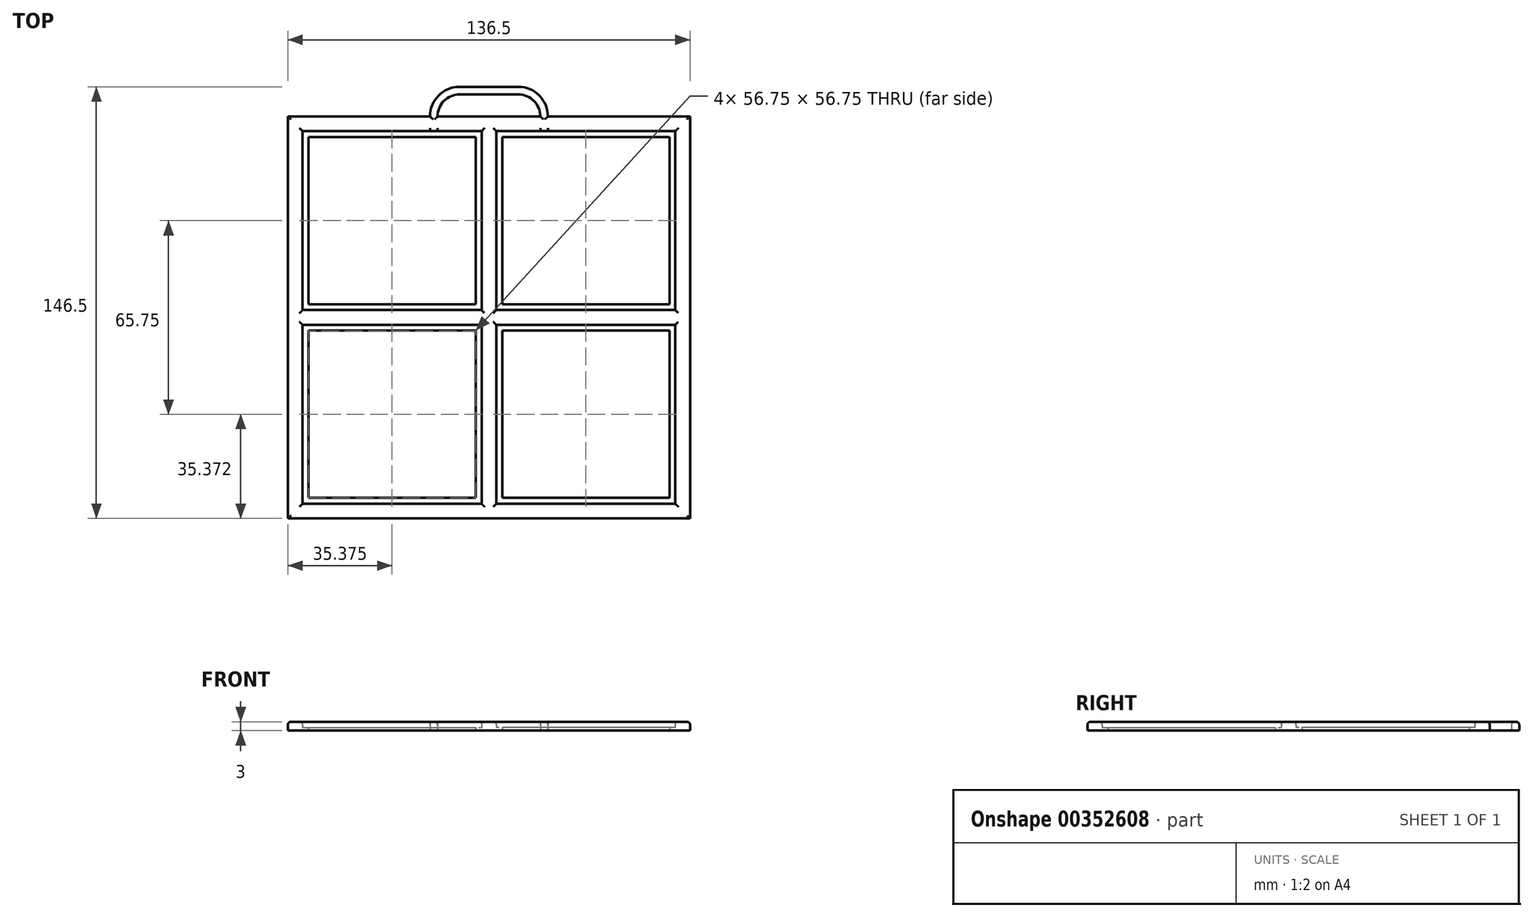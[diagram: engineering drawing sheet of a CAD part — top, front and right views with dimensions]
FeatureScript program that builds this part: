
annotation { "Feature Type Name" : "Feature", "Feature Type Description" : "" }
export const myFeature = defineFeature(function(context is Context, id is Id, definition is map)
    precondition{}
    {
        {
            var Q0;
            Q0=qCreatedBy(makeId("Top.planeOp"),FACE);
            var sketch = newSketch(context, id + "F0", { "sketchPlane" : qUnion([Q0])});
            skLineSegment(sketch, "E0.bottom", {"start": v(-63.25, 26.55) * mm, "end": v(-2.5, 26.55) * mm});
            skLineSegment(sketch, "E0.top", {"start": v(-63.25, -34.2) * mm, "end": v(-2.5, -34.2) * mm});
            skLineSegment(sketch, "E0.left", {"start": v(-63.25, 26.55) * mm, "end": v(-63.25, -34.2) * mm});
            skLineSegment(sketch, "E0.right", {"start": v(-2.5, 26.55) * mm, "end": v(-2.5, -34.2) * mm});
            skPoint(sketch, "E1", {"position": v(-2.5, 26.55) * mm});
            skPoint(sketch, "E2", {"position": v(-2.5, 31.55) * mm});
            skPoint(sketch, "E3", {"position": v(-2.5, -34.2) * mm});
            skPoint(sketch, "E4", {"position": v(-2.5, -36.7) * mm});
            skPoint(sketch, "E5", {"position": v(-63.25, -36.7) * mm});
            skPoint(sketch, "E6", {"position": v(-63.25, 31.55) * mm});
            skPoint(sketch, "E7", {"position": v(-63.25, 26.55) * mm});
            skPoint(sketch, "E8", {"position": v(-68.25, 26.55) * mm});
            skPoint(sketch, "E9", {"position": v(-68.25, 31.55) * mm});
            skPoint(sketch, "E10", {"position": v(0, -36.7) * mm});
            skLineSegment(sketch, "E11.bottom", {"start": v(-68.25, 31.55) * mm, "end": v(-20, 31.55) * mm});
            skLineSegment(sketch, "E11.top", {"start": v(-68.25, -36.7) * mm, "end": v(0, -36.7) * mm});
            skLineSegment(sketch, "E11.left", {"start": v(-68.25, 31.55) * mm, "end": v(-68.25, -36.7) * mm});
            skLineSegment(sketch, "E11.right", {"start": v(0, 31.55) * mm, "end": v(0, -36.7) * mm});
            skPoint(sketch, "E12", {"position": v(-34.12, 31.55) * mm});
            skPoint(sketch, "E13", {"position": v(-34.12, 41.55) * mm});
            skLineSegment(sketch, "E14", {"start": v(-34.12, 41.55) * mm, "end": v(-34.12, 31.55) * mm});
            skPoint(sketch, "E15", {"position": v(-34.12, 36.55) * mm});
            skPoint(sketch, "E16", {"position": v(-34.12, 38.98) * mm});
            skPoint(sketch, "E17", {"position": v(-61.25, 26.55) * mm});
            skPoint(sketch, "E18", {"position": v(-63.25, 24.55) * mm});
            skPoint(sketch, "E19", {"position": v(-61.25, 24.55) * mm});
            skPoint(sketch, "E20", {"position": v(-2.5, -32.2) * mm});
            skPoint(sketch, "E21", {"position": v(-4.5, -34.2) * mm});
            skPoint(sketch, "E22", {"position": v(-4.5, -32.2) * mm});
            skLineSegment(sketch, "E23.bottom", {"start": v(-61.25, 24.55) * mm, "end": v(-4.5, 24.55) * mm});
            skLineSegment(sketch, "E23.top", {"start": v(-61.25, -32.2) * mm, "end": v(-4.5, -32.2) * mm});
            skLineSegment(sketch, "E23.left", {"start": v(-61.25, 24.55) * mm, "end": v(-61.25, -32.2) * mm});
            skLineSegment(sketch, "E23.right", {"start": v(-4.5, 24.55) * mm, "end": v(-4.5, -32.2) * mm});
            skPoint(sketch, "E24", {"position": v(-10, 31.55) * mm});
            skLineSegment(sketch, "E25", {"start": v(0, 38.98) * mm, "end": v(0, 41.55) * mm});
            skPoint(sketch, "E26", {"position": v(-10, 38.98) * mm});
            skPoint(sketch, "E27", {"position": v(-10, 41.55) * mm});
            skArc(sketch, "E28", {"start": v(-10, 38.98) * mm, "mid": v(-15.25, 36.8) * mm, "end": v(-17.43, 31.55) * mm});
            skArc(sketch, "E29", {"start": v(-10, 41.55) * mm, "mid": v(-17.07, 38.62) * mm, "end": v(-20, 31.55) * mm});
            skLineSegment(sketch, "E30", {"start": v(-10, 38.98) * mm, "end": v(0, 38.98) * mm});
            skLineSegment(sketch, "E31", {"start": v(-10, 41.55) * mm, "end": v(0, 41.55) * mm});
            skLineSegment(sketch, "E32", {"start": v(-20, 31.55) * mm, "end": v(-17.43, 31.55) * mm});
            skLineSegment(sketch, "E33", {"start": v(-17.43, 31.55) * mm, "end": v(0, 31.55) * mm});
            skLineSegment(sketch, "E34", {"start": v(-20, 31.55) * mm, "end": v(-20, 26.55) * mm});
            skLineSegment(sketch, "E35", {"start": v(-20, 26.55) * mm, "end": v(-17.43, 26.55) * mm});
            skLineSegment(sketch, "E36", {"start": v(-17.43, 26.55) * mm, "end": v(-17.43, 31.55) * mm});
            skSolve(sketch);
        }
        {
            var Q0;
            Q0=makeQuery(id+"F0.imprint","IMPRINT",FACE,{"disambiguationData":[TD([[makeQuery(id+"F0.imprint","IMPRINT",EDGE,{"derivedFrom":sQuery(id+"F0.wireOp",EDGE,"E0.top")}),-1.0]])]});
            var Q1;
            {var subQ0=sQuery(id+"F0.wireOp",EDGE,"323iFSkM-69Tl-kqoX-bfbl-zxdwPlZIsCMZ");var subQ1=sQuery(id+"F0.wireOp",EDGE,"E0.bottom");var subQ2=makeQuery(id+"F0.imprint","INTERSECT",VERTEX,{"disambiguationData":[OD(0.0)],"derivedFrom":[subQ1,subQ0]});Q1=makeQuery(id+"F0.imprint","IMPRINT",FACE,{"disambiguationData":[TD([[makeQuery(id+"F0.imprint","IMPRINT",EDGE,{"disambiguationData":[TD([[subQ2,-1.0]])],"derivedFrom":subQ1}),1.0]])]});}
            var Q2;
            {var subQ0=sQuery(id+"F0.wireOp",EDGE,"S2f47POQ-odG1-F0nU-moLb-DiT50xx8mqJj");var subQ1=sQuery(id+"F0.wireOp",EDGE,"E0.bottom");var subQ2=makeQuery(id+"F0.imprint","INTERSECT",VERTEX,{"disambiguationData":[OD(1.0)],"derivedFrom":[subQ1,subQ0]});Q2=makeQuery(id+"F0.imprint","IMPRINT",FACE,{"disambiguationData":[TD([[makeQuery(id+"F0.imprint","IMPRINT",EDGE,{"disambiguationData":[TD([[subQ2,-1.0]])],"derivedFrom":subQ1}),1.0]])]});}
            var Q3;
            {var subQ0=sQuery(id+"F0.wireOp",EDGE,"S2f47POQ-odG1-F0nU-moLb-DiT50xx8mqJj");var subQ1=sQuery(id+"F0.wireOp",EDGE,"E0.bottom");var subQ2=makeQuery(id+"F0.imprint","INTERSECT",VERTEX,{"disambiguationData":[OD(0.0)],"derivedFrom":[subQ1,subQ0]});Q3=makeQuery(id+"F0.imprint","IMPRINT",FACE,{"disambiguationData":[TD([[makeQuery(id+"F0.imprint","IMPRINT",EDGE,{"disambiguationData":[TD([[subQ2,-1.0]])],"derivedFrom":subQ1}),1.0]])]});}
            var Q4;
            {var subQ0=sQuery(id+"F0.wireOp",EDGE,"RwKeYdOv-RQ1C-EBcZ-qULq-cMKYxm2aIbZM");var subQ1=sQuery(id+"F0.wireOp",EDGE,"E0.right");var subQ2=makeQuery(id+"F0.imprint","INTERSECT",VERTEX,{"derivedFrom":[subQ1,subQ0]});Q4=makeQuery(id+"F0.imprint","IMPRINT",FACE,{"disambiguationData":[TD([[makeQuery(id+"F0.imprint","IMPRINT",EDGE,{"disambiguationData":[TD([[subQ2,-1.0]])],"derivedFrom":subQ1}),1.0]])]});}
            var Q5;
            {var subQ6=sQuery(id+"F0.wireOp",EDGE,"E0.bottom");var subQ8=sQuery(id+"F0.wireOp",EDGE,"E0.right");var subQ9=makeQuery(id+"F0.imprint","INTERSECT",VERTEX,{"derivedFrom":[subQ6,subQ8]});Q5=makeQuery(id+"F0.imprint","IMPRINT",FACE,{"disambiguationData":[TD([[makeQuery(id+"F0.imprint","IMPRINT",EDGE,{"disambiguationData":[TD([[subQ9,1.0]])],"derivedFrom":subQ6}),1.0]])]});}
            var Q6;
            Q6=makeQuery(id+"F0.imprint","IMPRINT",FACE,{"disambiguationData":[TD([[makeQuery(id+"F0.imprint","IMPRINT",EDGE,{"derivedFrom":sQuery(id+"F0.wireOp",EDGE,"E32")}),-1.0]])]});
            extrude(context, id + "F1", {"entities" : qUnion([Q0, Q1, Q2, Q3, Q4, Q5, Q6]), "depth" : 3 * mm, "offsetDistance" : 25 * mm});
        }
        {
            var Q0;
            {var subQ0=sQuery(id+"F0.wireOp",EDGE,"S2f47POQ-odG1-F0nU-moLb-DiT50xx8mqJj");var subQ1=sQuery(id+"F0.wireOp",EDGE,"E0.bottom");var subQ2=makeQuery(id+"F0.imprint","INTERSECT",VERTEX,{"disambiguationData":[OD(0.0)],"derivedFrom":[subQ1,subQ0]});Q0=makeQuery(id+"F0.imprint","IMPRINT",FACE,{"disambiguationData":[TD([[makeQuery(id+"F0.imprint","IMPRINT",EDGE,{"disambiguationData":[TD([[subQ2,-1.0]])],"derivedFrom":subQ1}),-1.0]])]});}
            var Q1;
            {var subQ0=sQuery(id+"F0.wireOp",EDGE,"323iFSkM-69Tl-kqoX-bfbl-zxdwPlZIsCMZ");var subQ1=sQuery(id+"F0.wireOp",EDGE,"E0.bottom");var subQ2=makeQuery(id+"F0.imprint","INTERSECT",VERTEX,{"disambiguationData":[OD(0.0)],"derivedFrom":[subQ1,subQ0]});Q1=makeQuery(id+"F0.imprint","IMPRINT",FACE,{"disambiguationData":[TD([[makeQuery(id+"F0.imprint","IMPRINT",EDGE,{"disambiguationData":[TD([[subQ2,-1.0]])],"derivedFrom":subQ1}),-1.0]])]});}
            var Q2;
            {var subQ0=sQuery(id+"F0.wireOp",EDGE,"S2f47POQ-odG1-F0nU-moLb-DiT50xx8mqJj");var subQ1=sQuery(id+"F0.wireOp",EDGE,"E0.bottom");var subQ2=makeQuery(id+"F0.imprint","INTERSECT",VERTEX,{"disambiguationData":[OD(1.0)],"derivedFrom":[subQ1,subQ0]});Q2=makeQuery(id+"F0.imprint","IMPRINT",FACE,{"disambiguationData":[TD([[makeQuery(id+"F0.imprint","IMPRINT",EDGE,{"disambiguationData":[TD([[subQ2,-1.0]])],"derivedFrom":subQ1}),-1.0]])]});}
            var Q3;
            Q3=makeQuery(id+"F0.imprint","IMPRINT",FACE,{"disambiguationData":[TD([[makeQuery(id+"F0.imprint","IMPRINT",EDGE,{"derivedFrom":sQuery(id+"F0.wireOp",EDGE,"E0.top")}),1.0]])]});
            var Q4;
            {var subQ3=sQuery(id+"F0.wireOp",EDGE,"oISM5f6R-s7pY-zFvx-TeqI-MK5FqsrAusou");var subQ10=sQuery(id+"F0.wireOp",EDGE,"E0.bottom");var subQ11=makeQuery(id+"F0.imprint","INTERSECT",VERTEX,{"derivedFrom":[subQ10,subQ3]});Q4=makeQuery(id+"F0.imprint","IMPRINT",FACE,{"disambiguationData":[TD([[makeQuery(id+"F0.imprint","IMPRINT",EDGE,{"disambiguationData":[TD([[subQ11,-1.0]])],"derivedFrom":subQ10}),-1.0]])]});}
            extrude(context, id + "F2", {"entities" : qUnion([Q0, Q1, Q2, Q3, Q4]), "operationType" : NewBodyOperationType.ADD, "depth" : 1 * mm});
        }
        {
            var Q0;
            Q0=makeQuery(id+"F1.opExtrude","CAP_EDGE",EDGE,{"disambiguationData":[OSD([sQuery(id+"F0.wireOp",EDGE,"E0.bottom")])],"isStart":false});
            var Q1;
            Q1=makeQuery(id+"F1.opExtrude","CAP_EDGE",EDGE,{"disambiguationData":[OSD([sQuery(id+"F0.wireOp",EDGE,"E0.left")])],"isStart":false});
            var Q2;
            Q2=makeQuery(id+"F1.opExtrude","CAP_EDGE",EDGE,{"disambiguationData":[OSD([sQuery(id+"F0.wireOp",EDGE,"E0.top")])],"isStart":false});
            var Q3;
            Q3=makeQuery(id+"F1.opExtrude","CAP_EDGE",EDGE,{"disambiguationData":[OSD([sQuery(id+"F0.wireOp",EDGE,"E0.right")])],"isStart":false});
            var Q4;
            {var subQ0=sQuery(id+"F0.wireOp",EDGE,"E11.bottom");var subQ1=makeQuery(id+"F0.imprint","IMPRINT",VERTEX,{"derivedFrom":subQ0});Q4=makeQuery(id+"F1.opExtrude","CAP_EDGE",EDGE,{"disambiguationData":[OSD([subQ0]),TDD([makeQuery(id+"F0.imprint","IMPRINT",EDGE,{"disambiguationData":[TD([[subQ1,1.0]])],"derivedFrom":subQ0}),makeQuery(id+"F0.imprint","IMPRINT",EDGE,{"disambiguationData":[TD([[subQ1,-1.0]])],"derivedFrom":subQ0})])],"isStart":false});}
            var Q5;
            Q5=makeQuery(id+"F1.opExtrude","CAP_EDGE",EDGE,{"disambiguationData":[OSD([sQuery(id+"F0.wireOp",EDGE,"E11.left")])],"isStart":false});
            var Q6;
            Q6=makeQuery(id+"F1.opExtrude","CAP_EDGE",EDGE,{"disambiguationData":[OSD([sQuery(id+"F0.wireOp",EDGE,"oISM5f6R-s7pY-zFvx-TeqI-MK5FqsrAusou")])],"isStart":false});
            var Q7;
            Q7=makeQuery(id+"F1.opExtrude","CAP_EDGE",EDGE,{"disambiguationData":[OSD([sQuery(id+"F0.wireOp",EDGE,"RwKeYdOv-RQ1C-EBcZ-qULq-cMKYxm2aIbZM")])],"isStart":false});
            var Q8;
            {var subQ0=sQuery(id+"F0.wireOp",EDGE,"E11.bottom");Q8=makeQuery(id+"F1.opExtrude","CAP_EDGE",EDGE,{"disambiguationData":[OSD([subQ0]),TDD([makeQuery(id+"F0.imprint","IMPRINT",EDGE,{"disambiguationData":[TD([[makeQuery(id+"F0.imprint","INTERSECT",VERTEX,{"derivedFrom":[subQ0,sQuery(id+"F0.wireOp",EDGE,"RwKeYdOv-RQ1C-EBcZ-qULq-cMKYxm2aIbZM")]}),-1.0]])],"derivedFrom":subQ0})])],"isStart":false});}
            fillet(context, id + "F3", {"entities" : qUnion([Q0, Q1, Q2, Q3, Q4, Q5, Q6, Q7, Q8]), "radius" : 1 * mm, "tangentPropagation" : true, "allowEdgeOverflow" : false});
        }
        {
            var Q0;
            Q0=makeQuery(id+"F1.opExtrude","SWEPT_BODY",BODY,{"disambiguationData":[OSD([sQuery(id+"F0.wireOp",EDGE,"E0.bottom"),sQuery(id+"F0.wireOp",EDGE,"E0.top"),sQuery(id+"F0.wireOp",EDGE,"E0.left"),sQuery(id+"F0.wireOp",EDGE,"E0.right"),sQuery(id+"F0.wireOp",EDGE,"E11.bottom"),sQuery(id+"F0.wireOp",EDGE,"E11.top"),sQuery(id+"F0.wireOp",EDGE,"E11.left"),sQuery(id+"F0.wireOp",EDGE,"E11.right"),sQuery(id+"F0.wireOp",EDGE,"323iFSkM-69Tl-kqoX-bfbl-zxdwPlZIsCMZ"),sQuery(id+"F0.wireOp",EDGE,"S2f47POQ-odG1-F0nU-moLb-DiT50xx8mqJj")])]});
            var Q1;
            Q1=qCreatedBy(makeId("Right.planeOp"),FACE);
            mirror(context, id + "F4", {"operationType" : NewBodyOperationType.ADD, "entities" : qUnion([Q0]), "mirrorPlane" : qUnion([Q1])});
        }
        {
            var Q0;
            Q0=makeQuery(id+"F1.opExtrude","SWEPT_BODY",BODY,{"disambiguationData":[OSD([sQuery(id+"F0.wireOp",EDGE,"E0.bottom"),sQuery(id+"F0.wireOp",EDGE,"E0.top"),sQuery(id+"F0.wireOp",EDGE,"E0.left"),sQuery(id+"F0.wireOp",EDGE,"E0.right"),sQuery(id+"F0.wireOp",EDGE,"E11.bottom"),sQuery(id+"F0.wireOp",EDGE,"E11.top"),sQuery(id+"F0.wireOp",EDGE,"E11.left"),sQuery(id+"F0.wireOp",EDGE,"E11.right"),sQuery(id+"F0.wireOp",EDGE,"YFA6sMg5-ooe4-pIfk-JmcR-r9i5VlROMLmz"),sQuery(id+"F0.wireOp",EDGE,"oISM5f6R-s7pY-zFvx-TeqI-MK5FqsrAusou"),sQuery(id+"F0.wireOp",EDGE,"RwKeYdOv-RQ1C-EBcZ-qULq-cMKYxm2aIbZM")])]});
            var Q1;
            {var subQ0=makeQuery(id+"F1.opExtrude","SWEPT_FACE",FACE,{"disambiguationData":[OSD([sQuery(id+"F0.wireOp",EDGE,"E11.top")])]});Q1=makeQuery(id+"F4.boolean.opBoolean","MERGE",FACE,{"derivedFrom":[subQ0,makeQuery(id+"F4.opPattern","COPY",FACE,{"derivedFrom":subQ0,"instanceName":"1"})]});}
            mirror(context, id + "F5", {"operationType" : NewBodyOperationType.ADD, "entities" : qUnion([Q0]), "mirrorPlane" : qUnion([Q1])});
        }
        {
            var Q0;
            Q0=makeQuery(id+"F0.imprint","IMPRINT",FACE,{"disambiguationData":[TD([[makeQuery(id+"F0.imprint","IMPRINT",EDGE,{"derivedFrom":sQuery(id+"F0.wireOp",EDGE,"E25")}),1.0]])]});
            var Q1;
            Q1=makeQuery(id+"F0.imprint","IMPRINT",FACE,{"disambiguationData":[TD([[makeQuery(id+"F0.imprint","IMPRINT",EDGE,{"derivedFrom":sQuery(id+"F0.wireOp",EDGE,"E32")}),-1.0]])]});
            extrude(context, id + "F6", {"entities" : qUnion([Q0, Q1]), "operationType" : NewBodyOperationType.ADD, "depth" : 3 * mm, "offsetDistance" : 25 * mm});
        }
        {
            var Q0;
            {var subQ0=makeQuery(id+"F6.opExtrude","CAP_EDGE",EDGE,{"disambiguationData":[OSD([sQuery(id+"F0.wireOp",EDGE,"E30")])],"isStart":false});Q0=makeQuery(id+"F4.boolean.opBoolean","MERGE",EDGE,{"derivedFrom":[subQ0,makeQuery(id+"F4.opPattern","COPY",EDGE,{"derivedFrom":subQ0,"instanceName":"1"})]});}
            var Q1;
            Q1=makeQuery(id+"F4.opPattern","COPY",EDGE,{"derivedFrom":makeQuery(id+"F6.opExtrude","CAP_EDGE",EDGE,{"disambiguationData":[OSD([sQuery(id+"F0.wireOp",EDGE,"E28")])],"isStart":false}),"instanceName":"1"});
            var Q2;
            Q2=makeQuery(id+"F6.opExtrude","CAP_EDGE",EDGE,{"disambiguationData":[OSD([sQuery(id+"F0.wireOp",EDGE,"E28")])],"isStart":false});
            var Q3;
            Q3=makeQuery(id+"F6.opExtrude","CAP_EDGE",EDGE,{"disambiguationData":[OSD([sQuery(id+"F0.wireOp",EDGE,"E29")])],"isStart":false});
            var Q4;
            Q4=makeQuery(id+"F6.opExtrude","CAP_EDGE",EDGE,{"disambiguationData":[OSD([sQuery(id+"F0.wireOp",EDGE,"E35")])],"isStart":false});
            fillet(context, id + "F7", {"entities" : qUnion([Q0, Q1, Q2, Q3, Q4]), "radius" : 1 * mm, "tangentPropagation" : true, "allowEdgeOverflow" : false});
        }
        {
            var Q0;
            Q0=makeQuery(id+"F1.opExtrude","SWEPT_BODY",BODY,{"disambiguationData":[OSD([sQuery(id+"F0.wireOp",EDGE,"E0.bottom"),sQuery(id+"F0.wireOp",EDGE,"E0.top"),sQuery(id+"F0.wireOp",EDGE,"E0.left"),sQuery(id+"F0.wireOp",EDGE,"E0.right"),sQuery(id+"F0.wireOp",EDGE,"E11.bottom"),sQuery(id+"F0.wireOp",EDGE,"E11.top"),sQuery(id+"F0.wireOp",EDGE,"E11.left"),sQuery(id+"F0.wireOp",EDGE,"E11.right"),sQuery(id+"F0.wireOp",EDGE,"E32"),sQuery(id+"F0.wireOp",EDGE,"E33"),sQuery(id+"F0.wireOp",EDGE,"E35")])]});
            var Q1;
            Q1=qCreatedBy(makeId("Right.planeOp"),FACE);
            mirror(context, id + "F8", {"operationType" : NewBodyOperationType.ADD, "entities" : qUnion([Q0]), "mirrorPlane" : qUnion([Q1])});
        }
    });
